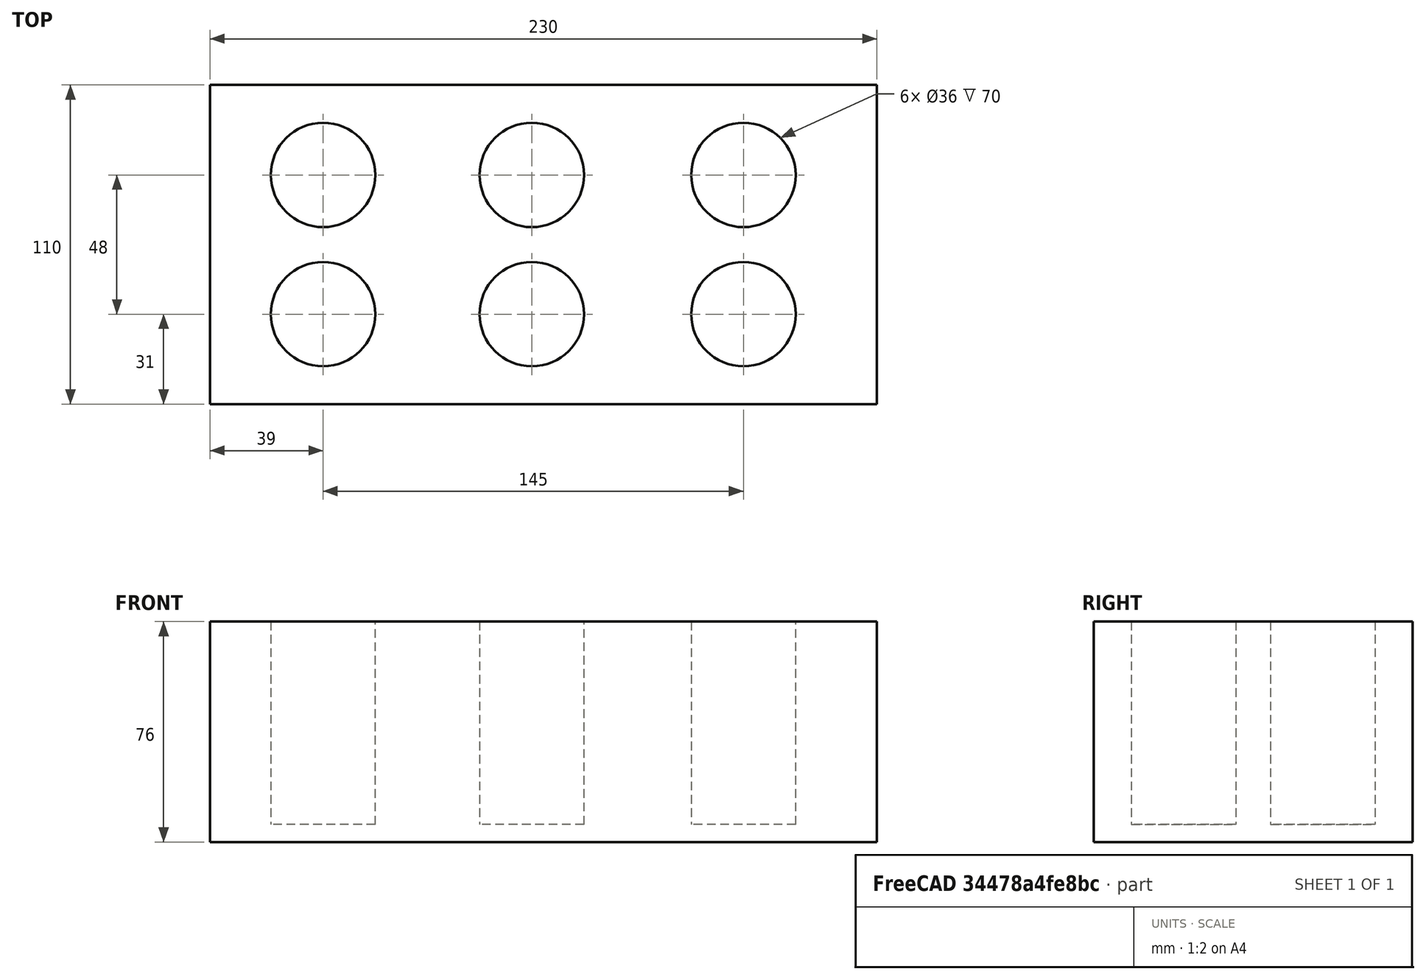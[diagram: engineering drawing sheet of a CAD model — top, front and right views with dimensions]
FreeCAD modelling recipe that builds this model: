
FCSTD DOCUMENT  (FreeCAD 1.0R39319 (Git))
Label: LADRILLO
License: All rights reserved
LicenseURL: https://en.wikipedia.org/wiki/All_rights_reserved
objects: Part::Cylinder×6, Part::MultiFuse×4, Part::Box×1, Part::Cut×1
note: 12 computed .brp shape members not serialized (recipe doc carries the construction recipe); baked Part::Feature solids carry a one-line shape summary decoded from their .brp

FEATURE [Part::Box] Box  label="Cube"
  AttacherType = Attacher::AttachEngine3D
  Height = 76
  Length = 230
  Width = 110
FEATURE [Part::Cylinder] Cylinder
  Angle = 360
  AttacherType = Attacher::AttachEngine3D
  FirstAngle = 0
  Height = 70
  Placement = pos=(39,31,6) rot=(0,0,1;0rad)
  Radius = 18
  SecondAngle = 0
FEATURE [Part::Cylinder] Cylinder001
  Angle = 360
  AttacherType = Attacher::AttachEngine3D
  FirstAngle = 0
  Height = 70
  Placement = pos=(39,79,6) rot=(0,0,1;0rad)
  Radius = 18
  SecondAngle = 0
FEATURE [Part::MultiFuse] Fusion
  Refine = true
  Shapes = -> [Cylinder,Cylinder001]
FEATURE [Part::Cylinder] Cylinder002
  Angle = 360
  AttacherType = Attacher::AttachEngine3D
  FirstAngle = 0
  Height = 70
  Placement = pos=(39,31,6) rot=(0,0,1;0rad)
  Radius = 18
  SecondAngle = 0
FEATURE [Part::Cylinder] Cylinder003
  Angle = 360
  AttacherType = Attacher::AttachEngine3D
  FirstAngle = 0
  Height = 70
  Placement = pos=(39,79,6) rot=(0,0,1;0rad)
  Radius = 18
  SecondAngle = 0
FEATURE [Part::MultiFuse] Fusion001
  Placement = pos=(72,0,0) rot=(0,0,1;0rad)
  Refine = true
  Shapes = -> [Cylinder002,Cylinder003]
FEATURE [Part::Cylinder] Cylinder004
  Angle = 360
  AttacherType = Attacher::AttachEngine3D
  FirstAngle = 0
  Height = 70
  Placement = pos=(39,31,6) rot=(0,0,1;0rad)
  Radius = 18
  SecondAngle = 0
FEATURE [Part::Cylinder] Cylinder005
  Angle = 360
  AttacherType = Attacher::AttachEngine3D
  FirstAngle = 0
  Height = 70
  Placement = pos=(39,79,6) rot=(0,0,1;0rad)
  Radius = 18
  SecondAngle = 0
FEATURE [Part::MultiFuse] Fusion002
  Placement = pos=(145,0,0) rot=(0,0,1;0rad)
  Refine = true
  Shapes = -> [Cylinder004,Cylinder005]
FEATURE [Part::MultiFuse] Fusion003
  Refine = true
  Shapes = -> [Fusion001,Fusion,Fusion002]
FEATURE [Part::Cut] Cut
  Base = -> Box
  Refine = true
  Tool = -> Fusion003
